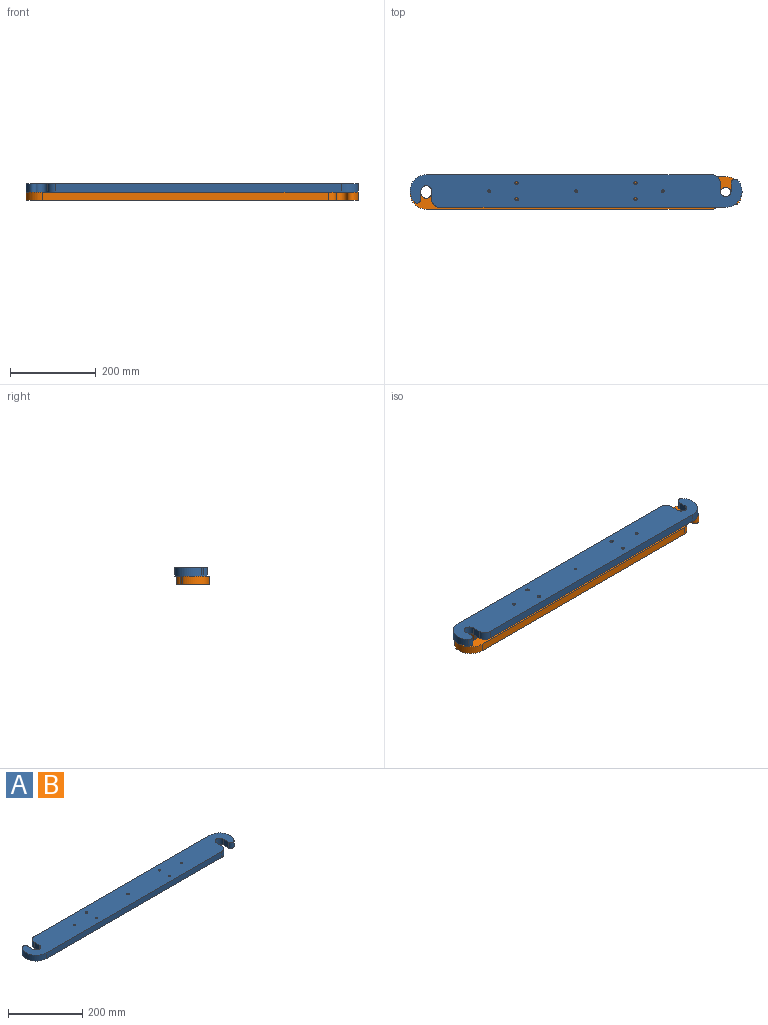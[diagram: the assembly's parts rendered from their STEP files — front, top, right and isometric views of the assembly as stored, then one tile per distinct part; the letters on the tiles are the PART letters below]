
ASSEMBLY  parts=2 mates=1
PART A: 23 faces, bbox 776.3x76.2x19.1 mm
  f0: cylinder r=12.7mm len=25.4mm, axis (0,0,-1), area 760.1mm2, adj f1,f19,f21,f22
  f1: plane 19.05x19.05mm, normal (1,0,0), area 362.9mm2, adj f0,f2,f21,f22
  f2: cylinder r=9.13mm len=19.05mm, axis (0,0,-1), area 421.5mm2, adj f1,f3,f21,f22
  f3: cylinder r=38.1mm len=63.15mm, axis (0,0,-1), area 1660.9mm2, adj f2,f4,f21,f22
  f4: plane 668.34x19.05mm, normal (0,-1,0), area 12731.8mm2, adj f3,f5,f21,f22
  f5: cylinder r=19.05mm len=19.05mm, axis (0,0,-1), area 570mm2, adj f4,f6,f21,f22
  f6: plane 19.05x19.05mm, normal (1,0,0), area 362.9mm2, adj f5,f7,f21,f22
  f7: cylinder r=12.7mm len=25.4mm, axis (0,0,-1), area 760.1mm2, adj f6,f8,f21,f22
  f8: plane 19.05x19.05mm, normal (-1,0,0), area 362.9mm2, adj f7,f9,f21,f22
  f9: cylinder r=9.13mm len=19.05mm, axis (0,0,-1), area 421.5mm2, adj f8,f10,f21,f22
  f10: cylinder r=38.1mm len=63.15mm, axis (0,0,-1), area 1660.9mm2, adj f9,f11,f21,f22
  f11: plane 668.34x19.05mm, normal (0,1,0), area 12731.8mm2, adj f10,f12,f21,f22
  f12: cylinder r=19.05mm len=19.05mm, axis (0,0,-1), area 570mm2, adj f11,f19,f21,f22
  f13: cylinder r=3.17mm len=19.05mm, axis (0,0,-1), area 380mm2, adj f21,f22
  f14: cylinder r=3.17mm len=19.05mm, axis (0,0,-1), area 380mm2, adj f21,f22
  f15: cylinder r=3.97mm len=19.05mm, axis (0,0,-1), area 475mm2, adj f21,f22
  f16: cylinder r=3.97mm len=19.05mm, axis (0,0,-1), area 475mm2, adj f21,f22
  f17: cylinder r=3.97mm len=19.05mm, axis (0,0,-1), area 475mm2, adj f21,f22
  f18: cylinder r=3.97mm len=19.05mm, axis (0,0,-1), area 475mm2, adj f21,f22
  f19: plane 19.05x19.05mm, normal (-1,0,0), area 362.9mm2, adj f0,f12,f21,f22
  f20: cylinder r=3.17mm len=19.05mm, axis (0,0,-1), area 380mm2, adj f21,f22
  f21: plane 776.29x76.2mm, normal (0,0,1), area 54879.2mm2, adj f0,f1,f2,f3,f4,f5,f6,f7
  f22: plane 776.29x76.2mm, normal (0,0,-1), area 54879.2mm2, adj f0,f1,f2,f3,f4,f5,f6,f7
PART B: same geometry as A
PLACE A rot(axis=(1,0,0),180deg) t=(-4.71,-12.57,83.44)mm
PLACE B t=(-4.71,12.56,-56.26)mm
MATE planar A.f20 <-> B.f20  axis (0,0,-1) through (-4.71,1.98,13.59)mm
